# Revit family: CADS_Vent-Axia_MechEquip_Fan_VSP_SabreSicklePlate_1Ph4P - SUPPLY
name_source: partatom
category: Mechanical Equipment
units: mm (PartAtom-declared; Revit-internal decimal feet)

## family parameters
Always vertical = Yes
Cut with Voids When Loaded = No
OmniClass Number = 23.75.00.00
OmniClass Title = Climate Control (HVAC)
Part Type = Normal
Room Calculation Point = No
Round Connector Dimension = Use Diameter
Shared = No
Work Plane-Based = No

## types (8) — shared parameters
AirflowRateRange = 0.0 L/s
AssemblyPlace = UNKNOWN
AssetType = FIXED
DurationUnit = Year
E = 34 mm
ExteriorInsulation = No
Fitting Type = Ignore
G = 17 mm
GrossWeight = 0.00 kg
HasProtectiveEarth = No
IfcExportAs = IfcFanType
IsExtendedWarranty = No
ManufacturerAddress = Fleming Way
Crawley 
RH10 9YX
Quantity = 1
RatedCurrent = 0 A
RatedVoltage = 0 V
Status = New
WarrantyGuarantor = Vent-Axia Limited
WorkingPressure = 0.0 Pa
zero-valued in all types: CADS_Index, CADS_Usage, Default Elevation, ExpectedServiceLife, NumberOfPoles

## per-type parameters (varying)
| type | A | ModelReference | NominalDiameter | NominalHeight | NominalLength | NominalWidth |
| VSP25014A | 370 mm  [stored 1.21391 ft] | OWLET SICKLE PLATE FAN 250 DIA 1PH 4 POLE | 250 mm  [stored 0.82021 ft] | 250 mm  [stored 0.82021 ft] | 73 mm | 370 mm  [stored 1.21391 ft] |
| VSP31514B | 430 mm | 315MM 1PH 4P SICKLE FAN FN031-4EQ.WD.A7 (169504) | 315 mm  [stored 1.03346 ft] | 315 mm  [stored 1.03346 ft] | 84 mm | 430 mm |
| VSP35514B | 485 mm  [stored 1.59121 ft] | 355MM 1PH 4P SICKLE FAN FN035-4EQ.WD.A7 (169505) | 355 mm | 355 mm | 83 mm | 485 mm  [stored 1.59121 ft] |
| VSP40014A | 549 mm  [stored 1.80118 ft] | OWLET SICKLE PLATE FAN 400DIA 1PH 4 POLE | 400 mm  [stored 1.31234 ft] | 400 mm  [stored 1.31234 ft] | 92 mm | 549 mm  [stored 1.80118 ft] |
| VSP45014B | 575 mm | 450MM 1PH 4P SICKLE FAN FN045-4EQ.4I.A7P1 169508 | 450 mm  [stored 1.47638 ft] | 450 mm  [stored 1.47638 ft] | 144 mm | 575 mm |
| VSP50014B | 655 mm  [stored 2.14895 ft] | 500MM 1PH 4P SICKLE FAN FN050-4EQ.4I.A7P1 169510 | 500 mm  [stored 1.64042 ft] | 500 mm  [stored 1.64042 ft] | 142 mm | 655 mm  [stored 2.14895 ft] |
| VSP56014B | 725 mm  [stored 2.37861 ft] | 560MM 1PH 4P SICKLE FAN FN056-4EQ.6K.A7P3 169513 | 560 mm  [stored 1.83727 ft] | 560 mm  [stored 1.83727 ft] | 168 mm | 725 mm  [stored 2.37861 ft] |
| VSP63014B | 725 mm  [stored 2.37861 ft] | 630MM 1PH 4P SICKLE FAN FN063-4EQ.6N.A7P6 169517 | 630 mm  [stored 2.06693 ft] | 630 mm  [stored 2.06693 ft] | 160 mm | 725 mm  [stored 2.37861 ft] |

note: column(s) folded — value = type name in every type: ModelNumber

note: [stored X ft] marks values corroborated as IEEE doubles in the binary element streams (Revit-internal decimal feet)

## geometry (parser evidence)
native form markers: Sweep x10
no freeform markers — native parametric forms only
